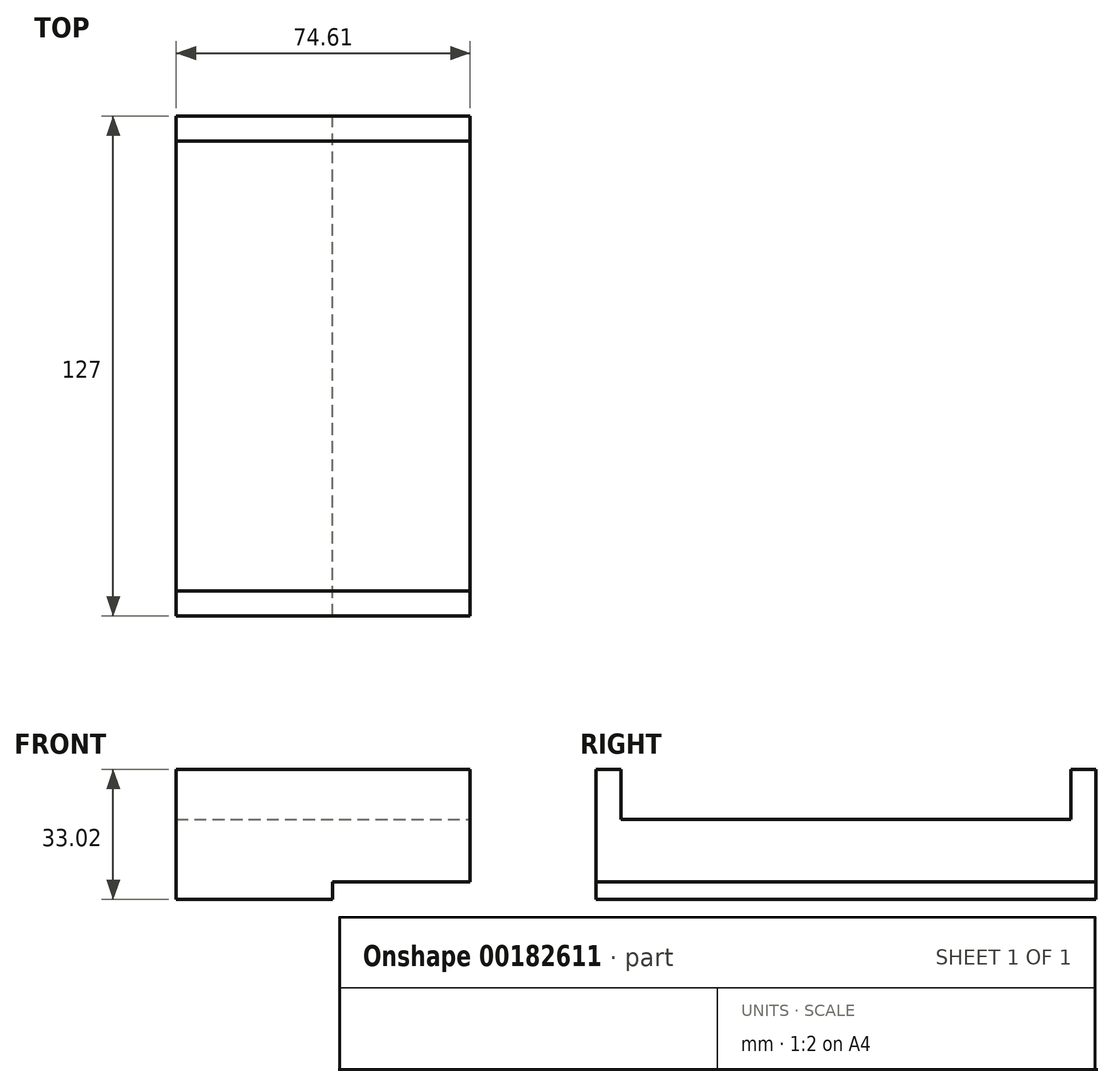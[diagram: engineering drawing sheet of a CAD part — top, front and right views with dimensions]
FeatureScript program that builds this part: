
annotation { "Feature Type Name" : "Feature", "Feature Type Description" : "" }
export const myFeature = defineFeature(function(context is Context, id is Id, definition is map)
    precondition{}
    {
        {
            var Q0;
            Q0=qCreatedBy(makeId("Front.planeOp"),FACE);
            var sketch = newSketch(context, id + "F0", { "sketchPlane" : qUnion([Q0])});
            skLineSegment(sketch, "E0", {"start": v(0, 0) * mm, "end": v(39.69, 0) * mm});
            skLineSegment(sketch, "E1", {"start": v(39.69, 0) * mm, "end": v(39.69, 4.45) * mm});
            skLineSegment(sketch, "E2", {"start": v(39.69, 4.45) * mm, "end": v(74.61, 4.45) * mm});
            skLineSegment(sketch, "E3", {"start": v(74.61, 4.45) * mm, "end": v(74.61, 20.32) * mm});
            skLineSegment(sketch, "E4", {"start": v(74.61, 20.32) * mm, "end": v(0, 20.32) * mm});
            skLineSegment(sketch, "E5", {"start": v(0, 20.32) * mm, "end": v(0, 0) * mm});
            skSolve(sketch);
        }
        {
            var Q0;
            Q0=makeQuery(id+"F0.imprint","IMPRINT",FACE,{"disambiguationData":[TD([[makeQuery(id+"F0.imprint","IMPRINT",EDGE,{"derivedFrom":sQuery(id+"F0.wireOp",EDGE,"E0")}),1.0]])]});
            extrude(context, id + "F1", {"entities" : qUnion([Q0]), "depth" : 127 * mm});
        }
        {
            var Q0;
            Q0=makeQuery(id+"F1.opExtrude","SWEPT_FACE",FACE,{"disambiguationData":[OSD([sQuery(id+"F0.wireOp",EDGE,"E4")])]});
            var sketch = newSketch(context, id + "F2", { "sketchPlane" : qUnion([Q0])});
            skLineSegment(sketch, "E6.bottom", {"start": v(0, -127) * mm, "end": v(74.61, -127) * mm});
            skLineSegment(sketch, "E6.top", {"start": v(0, -120.65) * mm, "end": v(74.61, -120.65) * mm});
            skLineSegment(sketch, "E6.left", {"start": v(0, -127) * mm, "end": v(0, -120.65) * mm});
            skLineSegment(sketch, "E6.right", {"start": v(74.61, -127) * mm, "end": v(74.61, -120.65) * mm});
            skLineSegment(sketch, "E7.bottom", {"start": v(0, 0) * mm, "end": v(74.61, 0) * mm});
            skLineSegment(sketch, "E7.top", {"start": v(0, -6.35) * mm, "end": v(74.61, -6.35) * mm});
            skLineSegment(sketch, "E7.left", {"start": v(0, 0) * mm, "end": v(0, -6.35) * mm});
            skLineSegment(sketch, "E7.right", {"start": v(74.61, 0) * mm, "end": v(74.61, -6.35) * mm});
            skSolve(sketch);
        }
        {
            var Q0;
            Q0=makeQuery(id+"F2.imprint","IMPRINT",FACE,{"disambiguationData":[TD([[makeQuery(id+"F2.imprint","IMPRINT",EDGE,{"derivedFrom":sQuery(id+"F2.wireOp",EDGE,"E6.bottom")}),-1.0]])]});
            var Q1;
            Q1=makeQuery(id+"F2.imprint","IMPRINT",FACE,{"disambiguationData":[TD([[makeQuery(id+"F2.imprint","IMPRINT",EDGE,{"derivedFrom":sQuery(id+"F2.wireOp",EDGE,"E7.bottom")}),1.0]])]});
            extrude(context, id + "F3", {"entities" : qUnion([Q0, Q1]), "operationType" : NewBodyOperationType.ADD, "depth" : 12.7 * mm});
        }
    });
